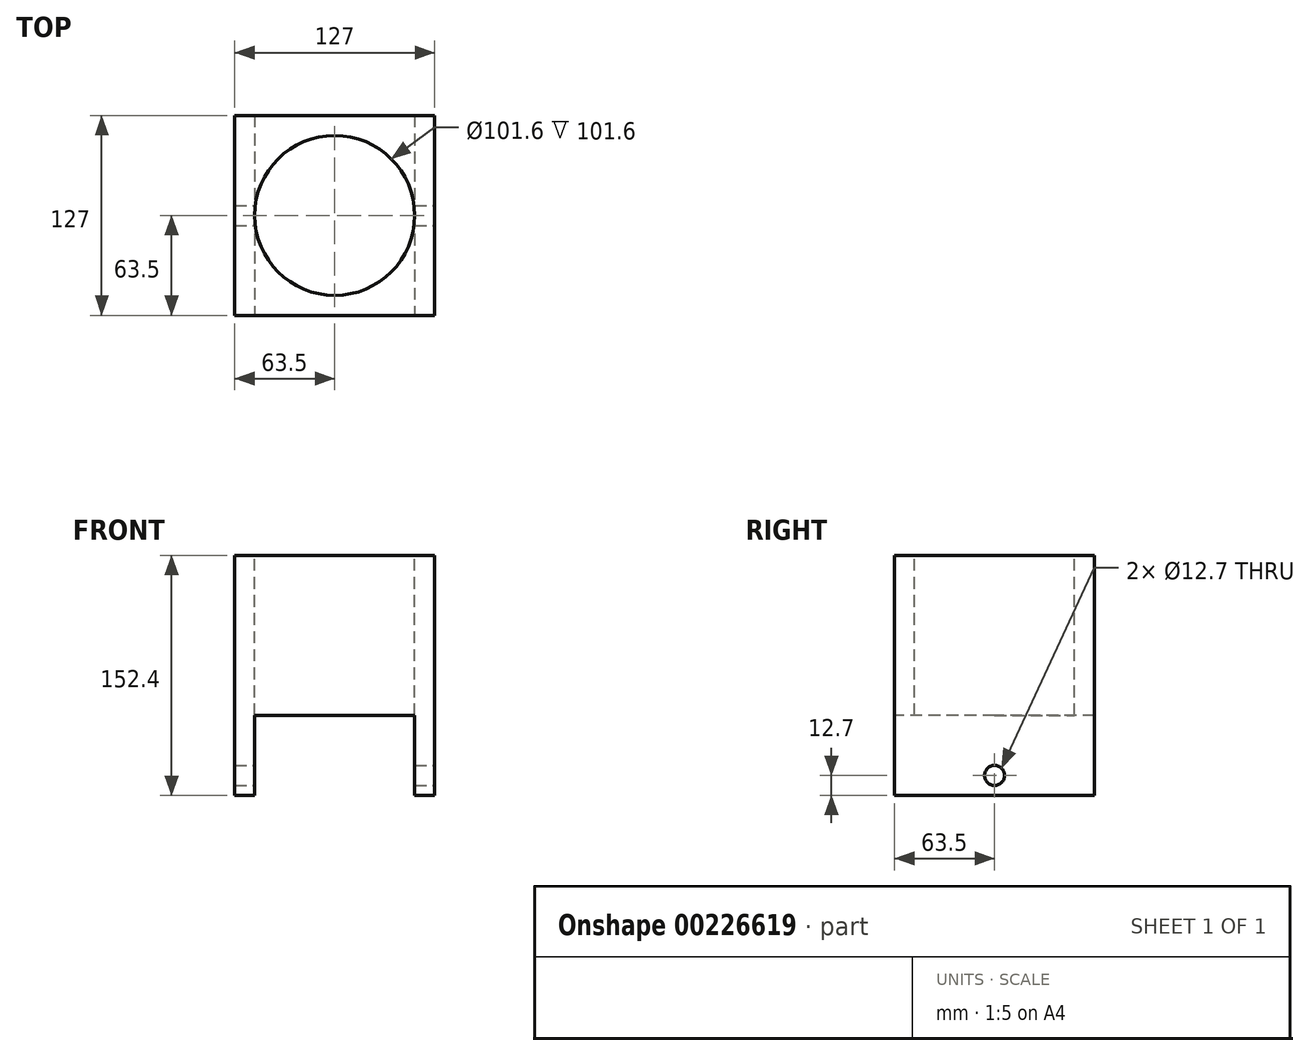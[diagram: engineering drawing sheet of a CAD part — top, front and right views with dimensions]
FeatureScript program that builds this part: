
annotation { "Feature Type Name" : "Feature", "Feature Type Description" : "" }
export const myFeature = defineFeature(function(context is Context, id is Id, definition is map)
    precondition{}
    {
        {
            var Q0;
            Q0=qCreatedBy(makeId("Top.planeOp"),FACE);
            var sketch = newSketch(context, id + "F0", { "sketchPlane" : qUnion([Q0])});
            skLineSegment(sketch, "E0.bottom", {"start": v(63.5, -63.5) * mm, "end": v(-63.5, -63.5) * mm});
            skLineSegment(sketch, "E0.top", {"start": v(63.5, 63.5) * mm, "end": v(-63.5, 63.5) * mm});
            skLineSegment(sketch, "E0.left", {"start": v(63.5, -63.5) * mm, "end": v(63.5, 63.5) * mm});
            skLineSegment(sketch, "E0.right", {"start": v(-63.5, -63.5) * mm, "end": v(-63.5, 63.5) * mm});
            skPoint(sketch, "E0.middle", {"position": v(0, 0) * mm});
            skSolve(sketch);
        }
        {
            var Q0;
            Q0 = qSketchRegion(id + "F0", true);
            extrude(context, id + "F1", {"entities" : qUnion([Q0]), "depth" : 152.4 * mm});
        }
        {
            var Q0;
            Q0=makeQuery(id+"F1.opExtrude","CAP_FACE",FACE,{"disambiguationData":[OSD([sQuery(id+"F0.wireOp",EDGE,"E0.bottom"),sQuery(id+"F0.wireOp",EDGE,"E0.top"),sQuery(id+"F0.wireOp",EDGE,"E0.left"),sQuery(id+"F0.wireOp",EDGE,"E0.right")])],"isStart":false});
            var sketch = newSketch(context, id + "F2", { "sketchPlane" : qUnion([Q0])});
            skCircle(sketch, "E1", {"center": v(0, 0) * mm, "radius": 50.8 * mm});
            skSolve(sketch);
        }
        {
            var Q0;
            Q0=makeQuery(id+"F2.imprint","IMPRINT",FACE,{"disambiguationData":[TD([[makeQuery(id+"F2.imprint","IMPRINT",EDGE,{"derivedFrom":sQuery(id+"F2.wireOp",EDGE,"E1")}),1.0]])]});
            extrude(context, id + "F3", {"entities" : qUnion([Q0]), "operationType" : NewBodyOperationType.REMOVE, "oppositeDirection" : true, "depth" : 127 * mm});
        }
        {
            var Q0;
            Q0=qCreatedBy(makeId("Front.planeOp"),FACE);
            var sketch = newSketch(context, id + "F4", { "sketchPlane" : qUnion([Q0])});
            skLineSegment(sketch, "E2.bottom", {"start": v(50.8, -68.9) * mm, "end": v(-50.8, -68.9) * mm});
            skLineSegment(sketch, "E2.top", {"start": v(50.8, 50.8) * mm, "end": v(-50.8, 50.8) * mm});
            skLineSegment(sketch, "E2.left", {"start": v(50.8, -68.9) * mm, "end": v(50.8, 50.8) * mm});
            skLineSegment(sketch, "E2.right", {"start": v(-50.8, -68.9) * mm, "end": v(-50.8, 50.8) * mm});
            skPoint(sketch, "E2.middle", {"position": v(0, -9.05) * mm});
            skSolve(sketch);
        }
        {
            var Q0;
            Q0 = qSketchRegion(id + "F4", true);
            extrude(context, id + "F5", {"entities" : qUnion([Q0]), "operationType" : NewBodyOperationType.REMOVE, "oppositeDirection" : true, "depth" : 127 * mm, "symmetric" : true});
        }
        {
            var Q0;
            Q0=makeQuery(id+"F1.opExtrude","SWEPT_FACE",FACE,{"disambiguationData":[OSD([sQuery(id+"F0.wireOp",EDGE,"E0.left")])]});
            var sketch = newSketch(context, id + "F6", { "sketchPlane" : qUnion([Q0])});
            skCircle(sketch, "E3", {"center": v(0, 12.7) * mm, "radius": 6.35 * mm});
            skPoint(sketch, "E3.centerSnap0", {"position": v(0, 0) * mm});
            skSolve(sketch);
        }
        {
            var Q0;
            Q0 = qSketchRegion(id + "F6", true);
            extrude(context, id + "F7", {"entities" : qUnion([Q0]), "operationType" : NewBodyOperationType.REMOVE, "oppositeDirection" : true, "depth" : 127 * mm});
        }
    });
